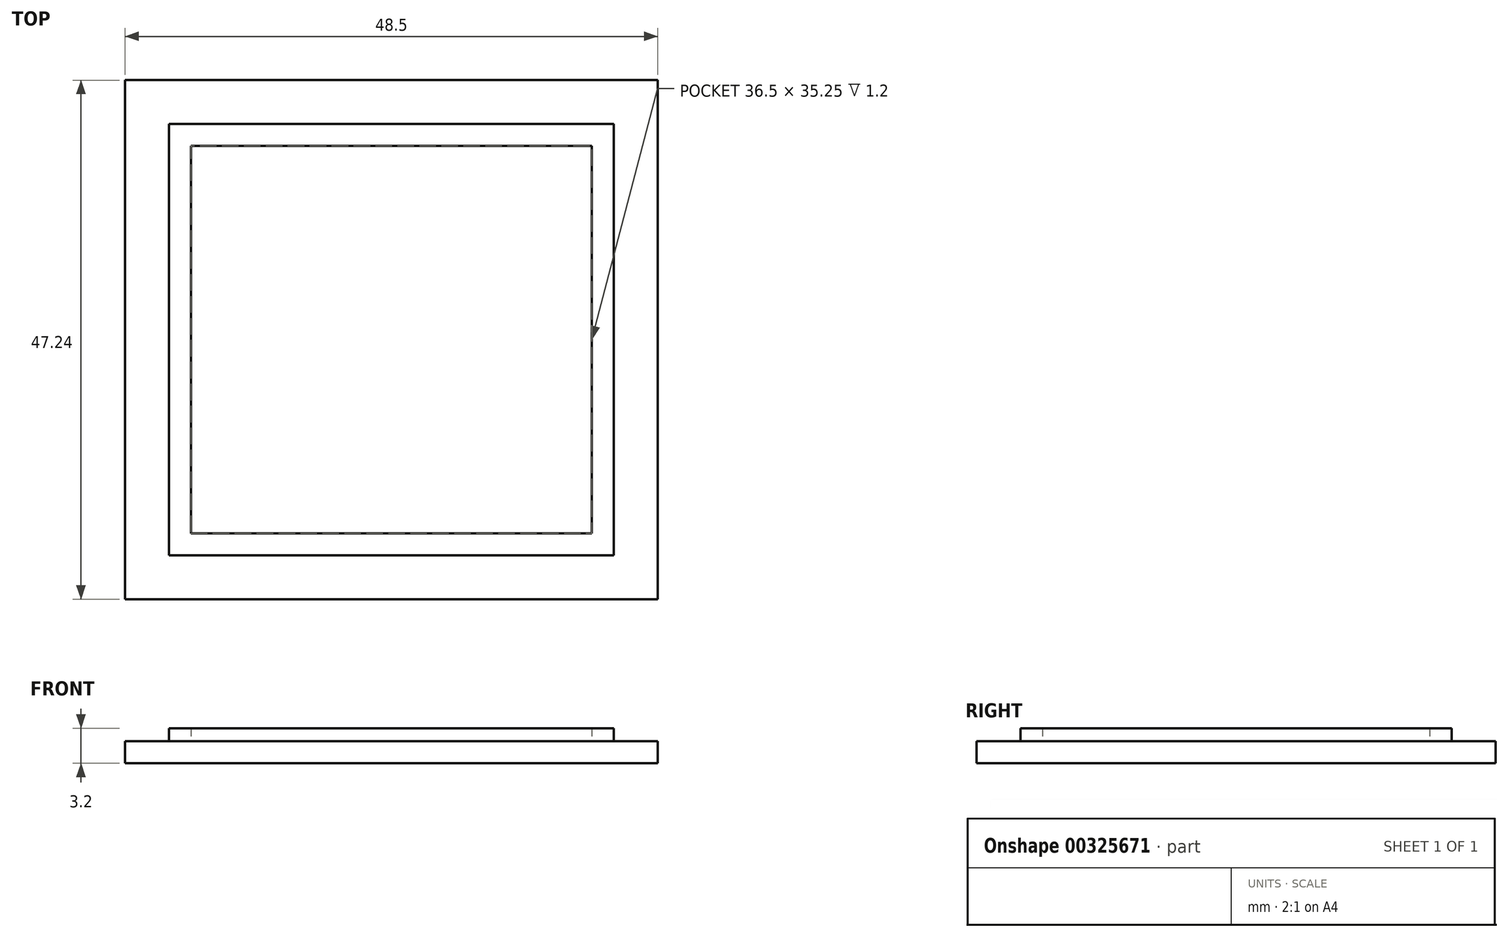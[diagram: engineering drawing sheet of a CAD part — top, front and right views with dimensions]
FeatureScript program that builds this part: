
annotation { "Feature Type Name" : "Feature", "Feature Type Description" : "" }
export const myFeature = defineFeature(function(context is Context, id is Id, definition is map)
    precondition{}
    {
        {
            var Q0;
            Q0=qCreatedBy(makeId("Top.planeOp"),FACE);
            var sketch = newSketch(context, id + "F0", { "sketchPlane" : qUnion([Q0])});
            skLineSegment(sketch, "E0.bottom", {"start": v(18.25, 17.62) * mm, "end": v(-18.25, 17.62) * mm});
            skLineSegment(sketch, "E0.top", {"start": v(18.25, -17.62) * mm, "end": v(-18.25, -17.62) * mm});
            skLineSegment(sketch, "E0.left", {"start": v(18.25, 17.62) * mm, "end": v(18.25, -17.63) * mm});
            skLineSegment(sketch, "E0.right", {"start": v(-18.25, 17.62) * mm, "end": v(-18.25, -17.63) * mm});
            skPoint(sketch, "E0.middle", {"position": v(0, 0) * mm});
            skLineSegment(sketch, "E1.bottom", {"start": v(20.25, -19.62) * mm, "end": v(-20.25, -19.62) * mm});
            skLineSegment(sketch, "E1.top", {"start": v(20.25, 19.62) * mm, "end": v(-20.25, 19.62) * mm});
            skLineSegment(sketch, "E1.left", {"start": v(20.25, -19.63) * mm, "end": v(20.25, 19.63) * mm});
            skLineSegment(sketch, "E1.right", {"start": v(-20.25, -19.63) * mm, "end": v(-20.25, 19.62) * mm});
            skLineSegment(sketch, "E2.bottom", {"start": v(24.25, -23.63) * mm, "end": v(-24.25, -23.63) * mm});
            skLineSegment(sketch, "E2.top", {"start": v(24.25, 23.63) * mm, "end": v(-24.25, 23.62) * mm});
            skLineSegment(sketch, "E2.left", {"start": v(24.25, -23.63) * mm, "end": v(24.25, 23.63) * mm});
            skLineSegment(sketch, "E2.right", {"start": v(-24.25, -23.63) * mm, "end": v(-24.25, 23.62) * mm});
            skSolve(sketch);
        }
        {
            var Q0;
            Q0=makeQuery(id+"F0.imprint","IMPRINT",FACE,{"disambiguationData":[TD([[makeQuery(id+"F0.imprint","IMPRINT",EDGE,{"derivedFrom":sQuery(id+"F0.wireOp",EDGE,"E1.bottom")}),1.0]])]});
            var Q1;
            Q1=makeQuery(id+"F0.imprint","IMPRINT",FACE,{"disambiguationData":[TD([[makeQuery(id+"F0.imprint","IMPRINT",EDGE,{"derivedFrom":sQuery(id+"F0.wireOp",EDGE,"E0.bottom")}),1.0]])]});
            var Q2;
            Q2=makeQuery(id+"F0.imprint","IMPRINT",FACE,{"disambiguationData":[TD([[makeQuery(id+"F0.imprint","IMPRINT",EDGE,{"derivedFrom":sQuery(id+"F0.wireOp",EDGE,"E0.bottom")}),-1.0]])]});
            extrude(context, id + "F1", {"entities" : qUnion([Q0, Q1, Q2]), "depth" : 2 * mm});
        }
        {
            var Q0;
            Q0=makeQuery(id+"F0.imprint","IMPRINT",FACE,{"disambiguationData":[TD([[makeQuery(id+"F0.imprint","IMPRINT",EDGE,{"derivedFrom":sQuery(id+"F0.wireOp",EDGE,"E0.bottom")}),-1.0]])]});
            extrude(context, id + "F2", {"entities" : qUnion([Q0]), "operationType" : NewBodyOperationType.ADD, "depth" : 3.2 * mm});
        }
    });
